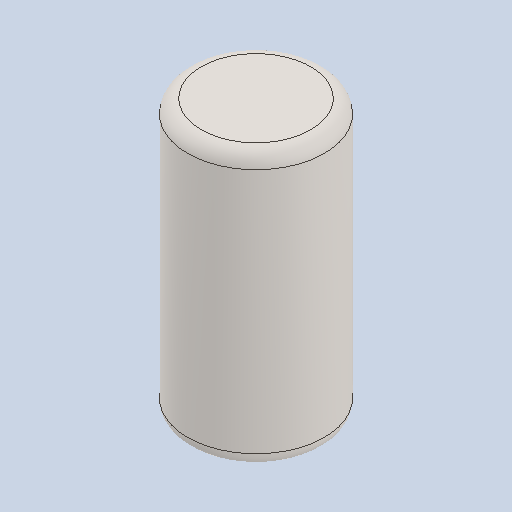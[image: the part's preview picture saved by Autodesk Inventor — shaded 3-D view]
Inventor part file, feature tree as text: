
AUTODESK INVENTOR PART (.ipt)
format: ipt  version: 2023.2 (Build 272271000, 271)  size: 102,400 bytes
history: native  units: in
note: dims shown in document units (in); Inventor stores cm internally (conversion verified against a paired STEP export)
features: fillet x1
ambient origin geometry x8: Origin, YZ Plane, XZ Plane, XY Plane, X Axis, Y Axis, Z Axis, Center Point
bodies: Solid1 (feature_tree)
feature tree (1):
  fillet  "Fillet1"  [1 undecoded]
note: 1 required parameter value undecoded (feature->parameter linkage not recoverable at this tier; creation-order binding heuristic only, values carry confidence <= 0.55)
